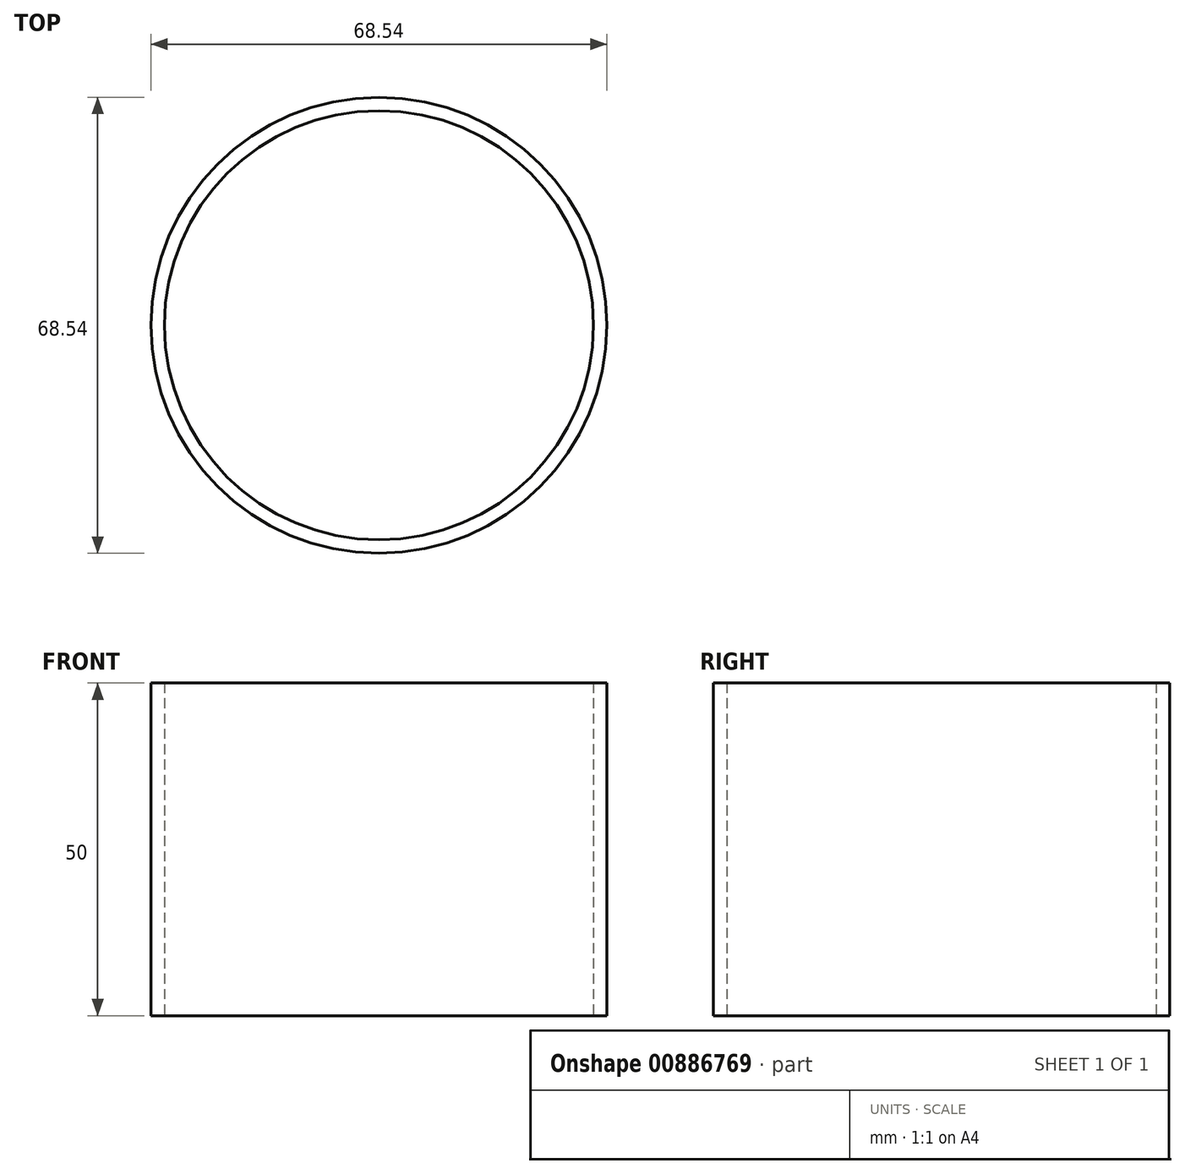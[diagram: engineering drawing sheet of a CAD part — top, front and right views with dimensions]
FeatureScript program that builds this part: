
annotation { "Feature Type Name" : "Feature", "Feature Type Description" : "" }
export const myFeature = defineFeature(function(context is Context, id is Id, definition is map)
    precondition{}
    {
        {
            var Q0;
            Q0=qCreatedBy(makeId("Top.planeOp"),FACE);
            var sketch = newSketch(context, id + "F0", { "sketchPlane" : qUnion([Q0])});
            skCircle(sketch, "E0", {"center": v(0, 0) * mm, "radius": 32.25 * mm});
            skCircle(sketch, "E1.0", {"center": v(0, 0) * mm, "radius": 34.27 * mm});
            skSolve(sketch);
        }
        {
            var Q0;
            Q0=makeQuery(id+"F0.imprint","IMPRINT",FACE,{"disambiguationData":[TD([[makeQuery(id+"F0.imprint","IMPRINT",EDGE,{"derivedFrom":sQuery(id+"F0.wireOp",EDGE,"E0")}),-1.0]])]});
            extrude(context, id + "F1", {"entities" : qUnion([Q0]), "depth" : 50 * mm, "offsetDistance" : 25 * mm});
        }
    });
